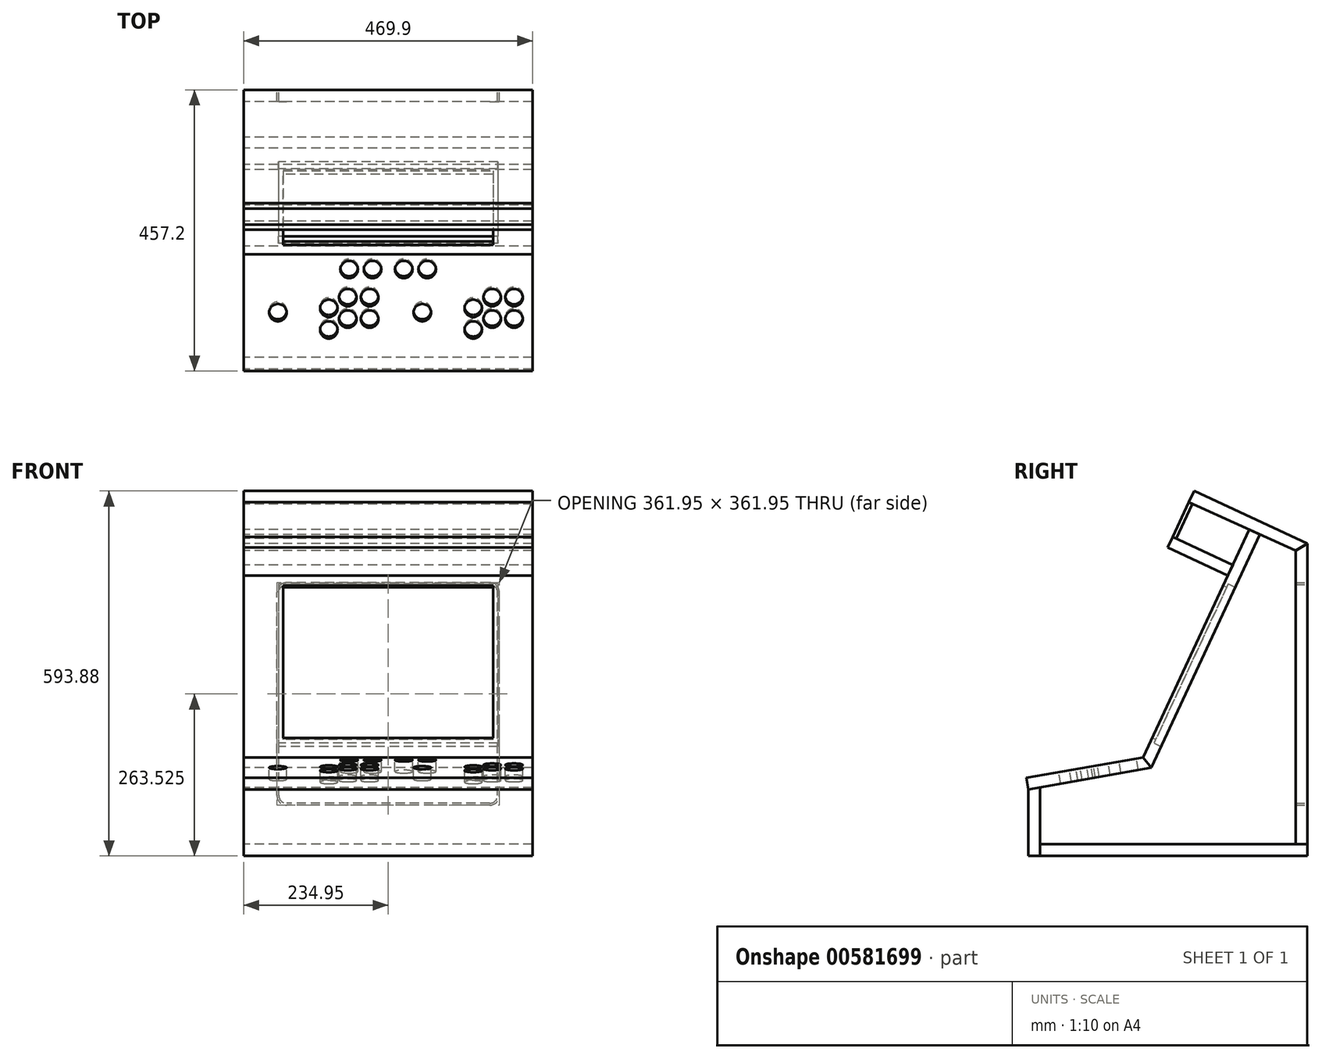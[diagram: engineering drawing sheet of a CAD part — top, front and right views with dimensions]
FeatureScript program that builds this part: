
annotation { "Feature Type Name" : "Feature", "Feature Type Description" : "" }
export const myFeature = defineFeature(function(context is Context, id is Id, definition is map)
    precondition{}
    {
        {
            var Q0;
            Q0=qCreatedBy(makeId("Right.planeOp"),FACE);
            var sketch = newSketch(context, id + "F0", { "sketchPlane" : qUnion([Q0])});
            skLineSegment(sketch, "E0.MirrorCS", {"start": v(273.04, 593.88) * mm, "end": v(230.1, 501.8) * mm, "construction": true});
            skLineSegment(sketch, "E1.MirrorCS", {"start": v(0, 593.88) * mm, "end": v(0, 127) * mm, "construction": true});
            skLineSegment(sketch, "E2.MirrorCS", {"start": v(273.04, 593.88) * mm, "end": v(0, 593.88) * mm, "construction": true});
            skLineSegment(sketch, "E3.MirrorCS", {"start": v(457.2, 508) * mm, "end": v(273.04, 593.88) * mm});
            skLineSegment(sketch, "E4", {"start": v(457.2, 0) * mm, "end": v(0, 0) * mm, "construction": true});
            skLineSegment(sketch, "E5", {"start": v(0, 0) * mm, "end": v(0, 127) * mm, "construction": true});
            skLineSegment(sketch, "E6", {"start": v(230.1, 501.8) * mm, "end": v(230.1, 593.88) * mm, "construction": true});
            skLineSegment(sketch, "E7", {"start": v(0, 127) * mm, "end": v(125.07, 149.05) * mm, "construction": true});
            skArc(sketch, "E8", {"start": v(125.07, 149.05) * mm, "mid": v(250.29, 303.78) * mm, "end": v(230.1, 501.8) * mm, "construction": true});
            skLineSegment(sketch, "E9.bottom", {"start": v(457.2, 19.05) * mm, "end": v(438.15, 19.05) * mm});
            skLineSegment(sketch, "E9.top", {"start": v(457.2, 508) * mm, "end": v(438.15, 497) * mm});
            skLineSegment(sketch, "E9.left", {"start": v(457.2, 19.05) * mm, "end": v(457.2, 508) * mm});
            skLineSegment(sketch, "E9.right", {"start": v(438.15, 19.05) * mm, "end": v(438.15, 497) * mm});
            skLineSegment(sketch, "E10", {"start": v(457.2, 0) * mm, "end": v(457.2, 19.05) * mm, "construction": true});
            skLineSegment(sketch, "E11", {"start": v(273.04, 593.88) * mm, "end": v(264.37, 575.28) * mm});
            skLineSegment(sketch, "E12", {"start": v(264.37, 575.28) * mm, "end": v(270.16, 572.68) * mm});
            skLineSegment(sketch, "E13", {"start": v(0, 0) * mm, "end": v(0, 19.05) * mm, "construction": true});
            skLineSegment(sketch, "E14", {"start": v(0, 127) * mm, "end": v(190.07, 160.51) * mm});
            skLineSegment(sketch, "E15", {"start": v(190.07, 160.51) * mm, "end": v(203.14, 143.48) * mm});
            skLineSegment(sketch, "E16", {"start": v(203.14, 143.48) * mm, "end": v(3.3, 108.24) * mm});
            skLineSegment(sketch, "E17", {"start": v(3.3, 108.24) * mm, "end": v(0, 127) * mm});
            skLineSegment(sketch, "E18.bottom", {"start": v(457.2, 19.05) * mm, "end": v(22.36, 19.05) * mm});
            skLineSegment(sketch, "E18.top", {"start": v(457.2, 0) * mm, "end": v(22.36, 0) * mm});
            skLineSegment(sketch, "E18.left", {"start": v(457.2, 19.05) * mm, "end": v(457.2, 0) * mm});
            skLineSegment(sketch, "E18.right", {"start": v(22.36, 19.05) * mm, "end": v(22.36, 0) * mm});
            skLineSegment(sketch, "E19.bottom", {"start": v(22.36, 0) * mm, "end": v(3.3, 0) * mm});
            skLineSegment(sketch, "E19.top", {"start": v(22.36, 111.6) * mm, "end": v(3.3, 108.24) * mm});
            skLineSegment(sketch, "E19.left", {"start": v(22.36, 0) * mm, "end": v(22.36, 111.6) * mm});
            skLineSegment(sketch, "E19.right", {"start": v(3.3, 0) * mm, "end": v(3.3, 108.24) * mm});
            skLineSegment(sketch, "E20", {"start": v(230.1, 501.8) * mm, "end": v(238.15, 519.06) * mm});
            skLineSegment(sketch, "E21", {"start": v(238.15, 519.06) * mm, "end": v(243.9, 516.38) * mm});
            skLineSegment(sketch, "E22", {"start": v(335.99, 473.44) * mm, "end": v(327.94, 456.17) * mm});
            skLineSegment(sketch, "E23", {"start": v(327.94, 456.17) * mm, "end": v(230.1, 501.8) * mm});
            skLineSegment(sketch, "E24", {"start": v(327.94, 456.17) * mm, "end": v(190.07, 160.51) * mm});
            skLineSegment(sketch, "E25", {"start": v(335.99, 473.44) * mm, "end": v(362.8, 530.94) * mm});
            skLineSegment(sketch, "E26", {"start": v(362.8, 530.94) * mm, "end": v(380.17, 523.12) * mm});
            skLineSegment(sketch, "E27", {"start": v(380.17, 523.12) * mm, "end": v(203.14, 143.48) * mm});
            skLineSegment(sketch, "E28", {"start": v(264.37, 575.28) * mm, "end": v(238.15, 519.06) * mm});
            skLineSegment(sketch, "E29", {"start": v(243.9, 516.38) * mm, "end": v(335.99, 473.44) * mm});
            skLineSegment(sketch, "E30", {"start": v(270.16, 572.68) * mm, "end": v(438.15, 497) * mm});
            skLineSegment(sketch, "E31", {"start": v(270.16, 572.68) * mm, "end": v(243.9, 516.38) * mm});
            skSolve(sketch);
        }
        {
            var Q0;
            Q0=makeQuery(id+"F0.imprint","IMPRINT",FACE,{"disambiguationData":[TD([[makeQuery(id+"F0.imprint","IMPRINT",EDGE,{"derivedFrom":sQuery(id+"F0.wireOp",EDGE,"E9.top")}),1.0]])]});
            extrude(context, id + "F1", {"entities" : qUnion([Q0]), "depth" : 469.9 * mm});
        }
        {
            var Q0;
            Q0=makeQuery(id+"F0.imprint","IMPRINT",FACE,{"disambiguationData":[TD([[makeQuery(id+"F0.imprint","IMPRINT",EDGE,{"derivedFrom":sQuery(id+"F0.wireOp",EDGE,"E3.MirrorCS")}),1.0]])]});
            extrude(context, id + "F2", {"entities" : qUnion([Q0]), "depth" : 469.9 * mm});
        }
        {
            var Q0;
            {var subQ1=sQuery(id+"F0.wireOp",EDGE,"E18.top");Q0=makeQuery(id+"F0.imprint","IMPRINT",FACE,{"disambiguationData":[TD([[makeQuery(id+"F0.imprint","IMPRINT",EDGE,{"derivedFrom":subQ1}),-1.0]])]});}
            extrude(context, id + "F3", {"entities" : qUnion([Q0]), "depth" : 469.9 * mm});
        }
        {
            var Q0;
            {var subQ3=sQuery(id+"F0.wireOp",EDGE,"E19.bottom");Q0=makeQuery(id+"F0.imprint","IMPRINT",FACE,{"disambiguationData":[TD([[makeQuery(id+"F0.imprint","IMPRINT",EDGE,{"derivedFrom":subQ3}),-1.0]])]});}
            extrude(context, id + "F4", {"entities" : qUnion([Q0]), "depth" : 469.9 * mm});
        }
        {
            var Q0;
            Q0=makeQuery(id+"F0.imprint","IMPRINT",FACE,{"disambiguationData":[TD([[makeQuery(id+"F0.imprint","IMPRINT",EDGE,{"derivedFrom":sQuery(id+"F0.wireOp",EDGE,"E14")}),-1.0]])]});
            extrude(context, id + "F5", {"entities" : qUnion([Q0]), "depth" : 469.9 * mm});
        }
        {
            var Q0;
            Q0=makeQuery(id+"F0.imprint","IMPRINT",FACE,{"disambiguationData":[TD([[makeQuery(id+"F0.imprint","IMPRINT",EDGE,{"derivedFrom":sQuery(id+"F0.wireOp",EDGE,"E15")}),1.0]])]});
            extrude(context, id + "F6", {"entities" : qUnion([Q0]), "depth" : 469.9 * mm});
        }
        {
            var Q0;
            Q0=makeQuery(id+"F0.imprint","IMPRINT",FACE,{"disambiguationData":[TD([[makeQuery(id+"F0.imprint","IMPRINT",EDGE,{"derivedFrom":sQuery(id+"F0.wireOp",EDGE,"E20")}),-1.0]])]});
            extrude(context, id + "F7", {"entities" : qUnion([Q0]), "depth" : 469.9 * mm});
        }
        {
            var Q0;
            Q0=makeQuery(id+"F0.imprint","IMPRINT",FACE,{"disambiguationData":[TD([[makeQuery(id+"F0.imprint","IMPRINT",EDGE,{"derivedFrom":sQuery(id+"F0.wireOp",EDGE,"E12")}),-1.0]])]});
            extrude(context, id + "F8", {"entities" : qUnion([Q0]), "depth" : 469.9 * mm});
        }
        {
            var Q0;
            Q0=makeQuery(id+"F5.opExtrude","SWEPT_FACE",FACE,{"disambiguationData":[OSD([sQuery(id+"F0.wireOp",EDGE,"E14")])]});
            var sketch = newSketch(context, id + "F9", { "sketchPlane" : qUnion([Q0])});
            skCircle(sketch, "E32", {"center": v(55.56, 118.55) * mm, "radius": 14.29 * mm});
            skLineSegment(sketch, "E33.bottom", {"start": v(15.88, 74.1) * mm, "end": v(95.25, 74.1) * mm});
            skLineSegment(sketch, "E33.top", {"start": v(15.88, 163) * mm, "end": v(95.25, 163) * mm});
            skLineSegment(sketch, "E33.left", {"start": v(15.87, 74.1) * mm, "end": v(15.87, 163) * mm});
            skLineSegment(sketch, "E33.right", {"start": v(95.25, 74.1) * mm, "end": v(95.25, 163) * mm});
            skPoint(sketch, "E34.positionSnap0", {"position": v(95.25, 118.55) * mm});
            skPoint(sketch, "E34.positionSnap1", {"position": v(55.56, 74.1) * mm});
            skCircle(sketch, "E35", {"center": v(138.43, 89.98) * mm, "radius": 14.29 * mm});
            skCircle(sketch, "E36", {"center": v(138.43, 125.54) * mm, "radius": 14.29 * mm});
            skCircle(sketch, "E37", {"center": v(204.79, 143.32) * mm, "radius": 14.29 * mm});
            skCircle(sketch, "E38", {"center": v(169.23, 107.76) * mm, "radius": 14.29 * mm});
            skCircle(sketch, "E39", {"center": v(169.23, 143.32) * mm, "radius": 14.29 * mm});
            skCircle(sketch, "E40", {"center": v(204.79, 107.76) * mm, "radius": 14.29 * mm});
            skLineSegment(sketch, "E41", {"start": v(138.43, 89.98) * mm, "end": v(138.43, 118.55) * mm, "construction": true});
            skLineSegment(sketch, "E42", {"start": v(55.56, 118.55) * mm, "end": v(138.43, 118.55) * mm, "construction": true});
            skLineSegment(sketch, "E43", {"start": v(138.43, 89.98) * mm, "end": v(138.43, 125.54) * mm, "construction": true});
            skLineSegment(sketch, "E44", {"start": v(138.43, 125.54) * mm, "end": v(169.23, 143.32) * mm, "construction": true});
            skLineSegment(sketch, "E45", {"start": v(169.23, 143.32) * mm, "end": v(204.79, 143.32) * mm, "construction": true});
            skLineSegment(sketch, "E46", {"start": v(204.79, 143.32) * mm, "end": v(204.79, 107.76) * mm, "construction": true});
            skLineSegment(sketch, "E47", {"start": v(169.23, 143.32) * mm, "end": v(169.23, 107.76) * mm, "construction": true});
            skLineSegment(sketch, "E48", {"start": v(138.43, 125.54) * mm, "end": v(169.23, 107.76) * mm, "construction": true});
            skPoint(sketch, "E49", {"position": v(219.08, 107.76) * mm});
            skLineSegment(sketch, "E50", {"start": v(15.88, 74.1) * mm, "end": v(219.07, 74.1) * mm, "construction": true});
            skPoint(sketch, "E51", {"position": v(117.47, 74.1) * mm});
            skPoint(sketch, "E52", {"position": v(15.87, 118.55) * mm});
            skLineSegment(sketch, "E53", {"start": v(0, 118.55) * mm, "end": v(234.95, 118.55) * mm, "construction": true});
            skLineSegment(sketch, "E54", {"start": v(234.95, 118.55) * mm, "end": v(469.9, 118.55) * mm, "construction": true});
            skLineSegment(sketch, "E55", {"start": v(117.47, 118.55) * mm, "end": v(117.47, 22.05) * mm, "construction": true});
            skLineSegment(sketch, "E56", {"start": v(352.43, 118.55) * mm, "end": v(352.43, 22.05) * mm, "construction": true});
            skCircle(sketch, "E57", {"center": v(290.51, 118.55) * mm, "radius": 14.29 * mm});
            skLineSegment(sketch, "E58.bottom", {"start": v(250.82, 74.1) * mm, "end": v(330.2, 74.1) * mm});
            skLineSegment(sketch, "E58.top", {"start": v(250.82, 163) * mm, "end": v(330.2, 163) * mm});
            skLineSegment(sketch, "E58.left", {"start": v(250.83, 74.1) * mm, "end": v(250.83, 163) * mm});
            skLineSegment(sketch, "E58.right", {"start": v(330.2, 74.1) * mm, "end": v(330.2, 163) * mm});
            skPoint(sketch, "E59.positionSnap0", {"position": v(330.2, 118.55) * mm});
            skPoint(sketch, "E59.positionSnap1", {"position": v(290.51, 74.1) * mm});
            skCircle(sketch, "E60", {"center": v(373.38, 89.98) * mm, "radius": 14.29 * mm});
            skCircle(sketch, "E61", {"center": v(373.38, 125.54) * mm, "radius": 14.29 * mm});
            skCircle(sketch, "E62", {"center": v(439.74, 143.32) * mm, "radius": 14.29 * mm});
            skCircle(sketch, "E63", {"center": v(404.18, 107.76) * mm, "radius": 14.29 * mm});
            skCircle(sketch, "E64", {"center": v(404.18, 143.32) * mm, "radius": 14.29 * mm});
            skCircle(sketch, "E65", {"center": v(439.74, 107.76) * mm, "radius": 14.29 * mm});
            skLineSegment(sketch, "E66", {"start": v(373.38, 89.98) * mm, "end": v(373.38, 118.55) * mm, "construction": true});
            skLineSegment(sketch, "E67", {"start": v(290.51, 118.55) * mm, "end": v(373.38, 118.55) * mm, "construction": true});
            skLineSegment(sketch, "E68", {"start": v(373.38, 89.98) * mm, "end": v(373.38, 125.54) * mm, "construction": true});
            skLineSegment(sketch, "E69", {"start": v(373.38, 125.54) * mm, "end": v(404.18, 143.32) * mm, "construction": true});
            skLineSegment(sketch, "E70", {"start": v(404.18, 143.32) * mm, "end": v(439.74, 143.32) * mm, "construction": true});
            skLineSegment(sketch, "E71", {"start": v(439.74, 143.32) * mm, "end": v(439.74, 107.76) * mm, "construction": true});
            skLineSegment(sketch, "E72", {"start": v(404.18, 143.32) * mm, "end": v(404.18, 107.76) * mm, "construction": true});
            skLineSegment(sketch, "E73", {"start": v(373.38, 125.54) * mm, "end": v(404.18, 107.76) * mm, "construction": true});
            skPoint(sketch, "E74", {"position": v(454.03, 107.76) * mm});
            skLineSegment(sketch, "E75", {"start": v(250.82, 74.1) * mm, "end": v(454.03, 74.1) * mm, "construction": true});
            skPoint(sketch, "E76", {"position": v(352.43, 74.1) * mm});
            skPoint(sketch, "E77", {"position": v(250.83, 118.55) * mm});
            skLineSegment(sketch, "E78", {"start": v(234.95, 22.05) * mm, "end": v(234.95, 118.55) * mm, "construction": true});
            skLineSegment(sketch, "E79", {"start": v(234.95, 215.05) * mm, "end": v(234.95, 118.55) * mm, "construction": true});
            skCircle(sketch, "E80", {"center": v(171.45, 189.65) * mm, "radius": 14.29 * mm});
            skLineSegment(sketch, "E81", {"start": v(234.95, 215.05) * mm, "end": v(234.95, 189.65) * mm, "construction": true});
            skLineSegment(sketch, "E82", {"start": v(234.95, 189.65) * mm, "end": v(260.35, 189.65) * mm, "construction": true});
            skLineSegment(sketch, "E83", {"start": v(260.35, 189.65) * mm, "end": v(298.45, 189.65) * mm, "construction": true});
            skLineSegment(sketch, "E84", {"start": v(234.95, 189.65) * mm, "end": v(209.55, 189.65) * mm, "construction": true});
            skLineSegment(sketch, "E85", {"start": v(209.55, 189.65) * mm, "end": v(171.45, 189.65) * mm, "construction": true});
            skCircle(sketch, "E86", {"center": v(209.55, 189.65) * mm, "radius": 14.29 * mm});
            skCircle(sketch, "E87", {"center": v(260.35, 189.65) * mm, "radius": 14.29 * mm});
            skCircle(sketch, "E88", {"center": v(298.45, 189.65) * mm, "radius": 14.29 * mm});
            skSolve(sketch);
        }
        {
            var Q0;
            Q0=makeQuery(id+"F9.imprint","IMPRINT",FACE,{"disambiguationData":[TD([[makeQuery(id+"F9.imprint","IMPRINT",EDGE,{"derivedFrom":sQuery(id+"F9.wireOp",EDGE,"E36")}),1.0]])]});
            var Q1;
            Q1=makeQuery(id+"F9.imprint","IMPRINT",FACE,{"disambiguationData":[TD([[makeQuery(id+"F9.imprint","IMPRINT",EDGE,{"derivedFrom":sQuery(id+"F9.wireOp",EDGE,"E35")}),1.0]])]});
            var Q2;
            Q2=makeQuery(id+"F9.imprint","IMPRINT",FACE,{"disambiguationData":[TD([[makeQuery(id+"F9.imprint","IMPRINT",EDGE,{"derivedFrom":sQuery(id+"F9.wireOp",EDGE,"E38")}),1.0]])]});
            var Q3;
            Q3=makeQuery(id+"F9.imprint","IMPRINT",FACE,{"disambiguationData":[TD([[makeQuery(id+"F9.imprint","IMPRINT",EDGE,{"derivedFrom":sQuery(id+"F9.wireOp",EDGE,"E39")}),1.0]])]});
            var Q4;
            Q4=makeQuery(id+"F9.imprint","IMPRINT",FACE,{"disambiguationData":[TD([[makeQuery(id+"F9.imprint","IMPRINT",EDGE,{"derivedFrom":sQuery(id+"F9.wireOp",EDGE,"E37")}),1.0]])]});
            var Q5;
            Q5=makeQuery(id+"F9.imprint","IMPRINT",FACE,{"disambiguationData":[TD([[makeQuery(id+"F9.imprint","IMPRINT",EDGE,{"derivedFrom":sQuery(id+"F9.wireOp",EDGE,"E40")}),1.0]])]});
            var Q6;
            Q6=makeQuery(id+"F9.imprint","IMPRINT",FACE,{"disambiguationData":[TD([[makeQuery(id+"F9.imprint","IMPRINT",EDGE,{"derivedFrom":sQuery(id+"F9.wireOp",EDGE,"E80")}),1.0]])]});
            var Q7;
            Q7=makeQuery(id+"F9.imprint","IMPRINT",FACE,{"disambiguationData":[TD([[makeQuery(id+"F9.imprint","IMPRINT",EDGE,{"derivedFrom":sQuery(id+"F9.wireOp",EDGE,"E86")}),1.0]])]});
            var Q8;
            Q8=makeQuery(id+"F9.imprint","IMPRINT",FACE,{"disambiguationData":[TD([[makeQuery(id+"F9.imprint","IMPRINT",EDGE,{"derivedFrom":sQuery(id+"F9.wireOp",EDGE,"E32")}),1.0]])]});
            var Q9;
            Q9=makeQuery(id+"F9.imprint","IMPRINT",FACE,{"disambiguationData":[TD([[makeQuery(id+"F9.imprint","IMPRINT",EDGE,{"derivedFrom":sQuery(id+"F9.wireOp",EDGE,"E87")}),1.0]])]});
            var Q10;
            Q10=makeQuery(id+"F9.imprint","IMPRINT",FACE,{"disambiguationData":[TD([[makeQuery(id+"F9.imprint","IMPRINT",EDGE,{"derivedFrom":sQuery(id+"F9.wireOp",EDGE,"E88")}),1.0]])]});
            var Q11;
            Q11=makeQuery(id+"F9.imprint","IMPRINT",FACE,{"disambiguationData":[TD([[makeQuery(id+"F9.imprint","IMPRINT",EDGE,{"derivedFrom":sQuery(id+"F9.wireOp",EDGE,"E57")}),1.0]])]});
            var Q12;
            Q12=makeQuery(id+"F9.imprint","IMPRINT",FACE,{"disambiguationData":[TD([[makeQuery(id+"F9.imprint","IMPRINT",EDGE,{"derivedFrom":sQuery(id+"F9.wireOp",EDGE,"E60")}),1.0]])]});
            var Q13;
            Q13=makeQuery(id+"F9.imprint","IMPRINT",FACE,{"disambiguationData":[TD([[makeQuery(id+"F9.imprint","IMPRINT",EDGE,{"derivedFrom":sQuery(id+"F9.wireOp",EDGE,"E61")}),1.0]])]});
            var Q14;
            Q14=makeQuery(id+"F9.imprint","IMPRINT",FACE,{"disambiguationData":[TD([[makeQuery(id+"F9.imprint","IMPRINT",EDGE,{"derivedFrom":sQuery(id+"F9.wireOp",EDGE,"E63")}),1.0]])]});
            var Q15;
            Q15=makeQuery(id+"F9.imprint","IMPRINT",FACE,{"disambiguationData":[TD([[makeQuery(id+"F9.imprint","IMPRINT",EDGE,{"derivedFrom":sQuery(id+"F9.wireOp",EDGE,"E64")}),1.0]])]});
            var Q16;
            Q16=makeQuery(id+"F9.imprint","IMPRINT",FACE,{"disambiguationData":[TD([[makeQuery(id+"F9.imprint","IMPRINT",EDGE,{"derivedFrom":sQuery(id+"F9.wireOp",EDGE,"E62")}),1.0]])]});
            var Q17;
            Q17=makeQuery(id+"F9.imprint","IMPRINT",FACE,{"disambiguationData":[TD([[makeQuery(id+"F9.imprint","IMPRINT",EDGE,{"derivedFrom":sQuery(id+"F9.wireOp",EDGE,"E65")}),1.0]])]});
            extrude(context, id + "F10", {"entities" : qUnion([Q0, Q1, Q2, Q3, Q4, Q5, Q6, Q7, Q8, Q9, Q10, Q11, Q12, Q13, Q14, Q15, Q16, Q17]), "operationType" : NewBodyOperationType.REMOVE, "oppositeDirection" : true, "depth" : 19.05 * mm});
        }
        {
            var Q0;
            Q0=makeQuery(id+"F6.opExtrude","SWEPT_FACE",FACE,{"disambiguationData":[OSD([sQuery(id+"F0.wireOp",EDGE,"E22"),sQuery(id+"F0.wireOp",EDGE,"E24"),sQuery(id+"F0.wireOp",EDGE,"E25")])]});
            var sketch = newSketch(context, id + "F11", { "sketchPlane" : qUnion([Q0])});
            skLineSegment(sketch, "E89", {"start": v(469.9, 430.16) * mm, "end": v(0, 430.16) * mm, "construction": true});
            skLineSegment(sketch, "E90", {"start": v(234.95, 634.52) * mm, "end": v(234.95, 225.8) * mm, "construction": true});
            skLineSegment(sketch, "E91.bottom", {"start": v(405.6, 533.78) * mm, "end": v(64.3, 533.78) * mm});
            skLineSegment(sketch, "E91.top", {"start": v(405.6, 260.73) * mm, "end": v(64.3, 260.73) * mm});
            skLineSegment(sketch, "E91.left", {"start": v(405.6, 533.78) * mm, "end": v(405.6, 260.73) * mm});
            skLineSegment(sketch, "E91.right", {"start": v(64.3, 533.78) * mm, "end": v(64.3, 260.73) * mm});
            skPoint(sketch, "E91.middle", {"position": v(234.95, 397.25) * mm});
            skPoint(sketch, "E92", {"position": v(234.95, 430.16) * mm});
            skSolve(sketch);
        }
        {
            var Q0;
            Q0=makeQuery(id+"F11.imprint","IMPRINT",FACE,{"disambiguationData":[TD([[makeQuery(id+"F11.imprint","IMPRINT",EDGE,{"derivedFrom":sQuery(id+"F11.wireOp",EDGE,"E91.bottom")}),1.0]])]});
            extrude(context, id + "F12", {"entities" : qUnion([Q0]), "operationType" : NewBodyOperationType.REMOVE, "oppositeDirection" : true, "depth" : 19.05 * mm});
        }
        {
            var Q0;
            Q0=makeQuery(id+"F1.opExtrude","SWEPT_FACE",FACE,{"disambiguationData":[OSD([sQuery(id+"F0.wireOp",EDGE,"E9.left")])]});
            var sketch = newSketch(context, id + "F13", { "sketchPlane" : qUnion([Q0])});
            skLineSegment(sketch, "E93", {"start": v(0, 19.05) * mm, "end": v(-469.9, 508) * mm, "construction": true});
            skLineSegment(sketch, "E94.bottom", {"start": v(-400.05, 85.73) * mm, "end": v(-69.85, 85.73) * mm});
            skLineSegment(sketch, "E94.top", {"start": v(-400.05, 441.33) * mm, "end": v(-69.85, 441.33) * mm});
            skLineSegment(sketch, "E94.left", {"start": v(-412.75, 98.43) * mm, "end": v(-412.75, 428.63) * mm});
            skLineSegment(sketch, "E94.right", {"start": v(-57.15, 98.43) * mm, "end": v(-57.15, 428.63) * mm});
            skPoint(sketch, "E94.middle", {"position": v(-234.95, 263.53) * mm});
            skPoint(sketch, "E95.visualSharp", {"position": v(-412.75, 441.33) * mm});
            skArc(sketch, "E95.filletArc", {"start": v(-400.05, 441.33) * mm, "mid": v(-409.03, 437.6) * mm, "end": v(-412.75, 428.63) * mm});
            skPoint(sketch, "E96.visualSharp", {"position": v(-57.15, 441.33) * mm});
            skArc(sketch, "E96.filletArc", {"start": v(-57.15, 428.63) * mm, "mid": v(-60.87, 437.6) * mm, "end": v(-69.85, 441.33) * mm});
            skPoint(sketch, "E97.visualSharp", {"position": v(-412.75, 85.73) * mm});
            skArc(sketch, "E97.filletArc", {"start": v(-412.75, 98.43) * mm, "mid": v(-409.03, 89.44) * mm, "end": v(-400.05, 85.73) * mm});
            skPoint(sketch, "E98.visualSharp", {"position": v(-57.15, 85.73) * mm});
            skArc(sketch, "E98.filletArc", {"start": v(-69.85, 85.73) * mm, "mid": v(-60.87, 89.44) * mm, "end": v(-57.15, 98.43) * mm});
            skArc(sketch, "E99.0", {"start": v(-69.85, 82.55) * mm, "mid": v(-58.62, 87.2) * mm, "end": v(-53.97, 98.43) * mm});
            skLineSegment(sketch, "E99.1", {"start": v(-400.05, 82.55) * mm, "end": v(-69.85, 82.55) * mm});
            skLineSegment(sketch, "E99.2", {"start": v(-53.97, 98.43) * mm, "end": v(-53.97, 428.63) * mm});
            skArc(sketch, "E99.3", {"start": v(-415.93, 98.43) * mm, "mid": v(-411.28, 87.2) * mm, "end": v(-400.05, 82.55) * mm});
            skArc(sketch, "E99.4", {"start": v(-53.97, 428.63) * mm, "mid": v(-58.62, 439.85) * mm, "end": v(-69.85, 444.5) * mm});
            skLineSegment(sketch, "E99.5", {"start": v(-400.05, 444.5) * mm, "end": v(-69.85, 444.5) * mm});
            skArc(sketch, "E99.6", {"start": v(-400.05, 444.5) * mm, "mid": v(-411.28, 439.85) * mm, "end": v(-415.93, 428.63) * mm});
            skLineSegment(sketch, "E99.7", {"start": v(-415.92, 98.43) * mm, "end": v(-415.92, 428.63) * mm});
            skSolve(sketch);
        }
        {
            var Q0;
            Q0=makeQuery(id+"F13.imprint","IMPRINT",FACE,{"disambiguationData":[TD([[makeQuery(id+"F13.imprint","IMPRINT",EDGE,{"derivedFrom":sQuery(id+"F13.wireOp",EDGE,"E94.bottom")}),-1.0]])]});
            extrude(context, id + "F14", {"entities" : qUnion([Q0]), "operationType" : NewBodyOperationType.REMOVE, "oppositeDirection" : true, "depth" : 19.05 * mm});
        }
        {
            var Q0;
            Q0=makeQuery(id+"F6.opExtrude","SWEPT_FACE",FACE,{"disambiguationData":[OSD([sQuery(id+"F0.wireOp",EDGE,"E27")])]});
            var sketch = newSketch(context, id + "F15", { "sketchPlane" : qUnion([Q0])});
            skLineSegment(sketch, "E100.0", {"start": v(-56.36, 540.13) * mm, "end": v(-56.36, 254.38) * mm});
            skLineSegment(sketch, "E101.0", {"start": v(-413.54, 540.13) * mm, "end": v(-413.54, 254.38) * mm});
            skLineSegment(sketch, "E102.0", {"start": v(-413.54, 540.13) * mm, "end": v(-56.36, 540.13) * mm});
            skLineSegment(sketch, "E103.0", {"start": v(-413.54, 254.38) * mm, "end": v(-56.36, 254.38) * mm});
            skSolve(sketch);
        }
        {
            var Q0;
            Q0=makeQuery(id+"F15.imprint","IMPRINT",FACE,{"disambiguationData":[TD([[makeQuery(id+"F15.imprint","IMPRINT",EDGE,{"derivedFrom":sQuery(id+"F15.wireOp",EDGE,"E100.0")}),-1.0]])]});
            extrude(context, id + "F16", {"entities" : qUnion([Q0]), "operationType" : NewBodyOperationType.REMOVE, "oppositeDirection" : true, "depth" : 12.7 * mm});
        }
    });
